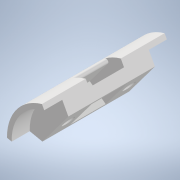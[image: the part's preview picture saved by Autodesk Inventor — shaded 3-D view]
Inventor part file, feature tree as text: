
AUTODESK INVENTOR PART (.ipt)
format: ipt  version: 2022 (Build 260153000, 153)  size: 197,120 bytes
history: native  units: mm
features: extrude x6, sketch x6, reference x6, other x5, projected_geometry x3, fillet x1
ambient origin geometry x8: Origin, YZ Plane, XZ Plane, XY Plane, X Axis, Y Axis, Z Axis, Center Point
bodies: Body1 (feature_tree)
feature tree (27):
  other  "Твердое тело1"
  extrude  "Выдавливание1"  Depth=0.2mm
  extrude  "Выдавливание2"  Depth=0.2mm
  extrude  "Выдавливание3"  Depth=34.0mm TaperAngle=0.0deg
  extrude  "Выдавливание4"  Depth=24.0mm TaperAngle=0.0deg
  fillet  "Сопряжение1"  Radius=2.5mm
  extrude  "Выдавливание5"  Depth=8.5mm
  extrude  "Выдавливание6"  Depth=4.95mm
  sketch  "Эскиз1"
  reference  "Ссылка1"
  reference  "Ссылка2"
  sketch  "Эскиз2"
  reference  "Ссылка3"
  reference  "Ссылка4"
  sketch  "Эскиз3"
  projected_geometry  "Спроецированная петля1"
  reference  "Ссылка5"
  sketch  "Эскиз4"
  projected_geometry  "Спроецированная петля2"
  sketch  "Эскиз5"
  reference  "Ссылка6"
  sketch  "Эскиз6"
  projected_geometry  "Спроецированная петля3"
  other  "<userpath>\Documents\Git\MZCAT_2024\MZCAT.iam"
  other  "MZCAT.iam"
  other  "base:1"
  other  "CAT_protector:1"
